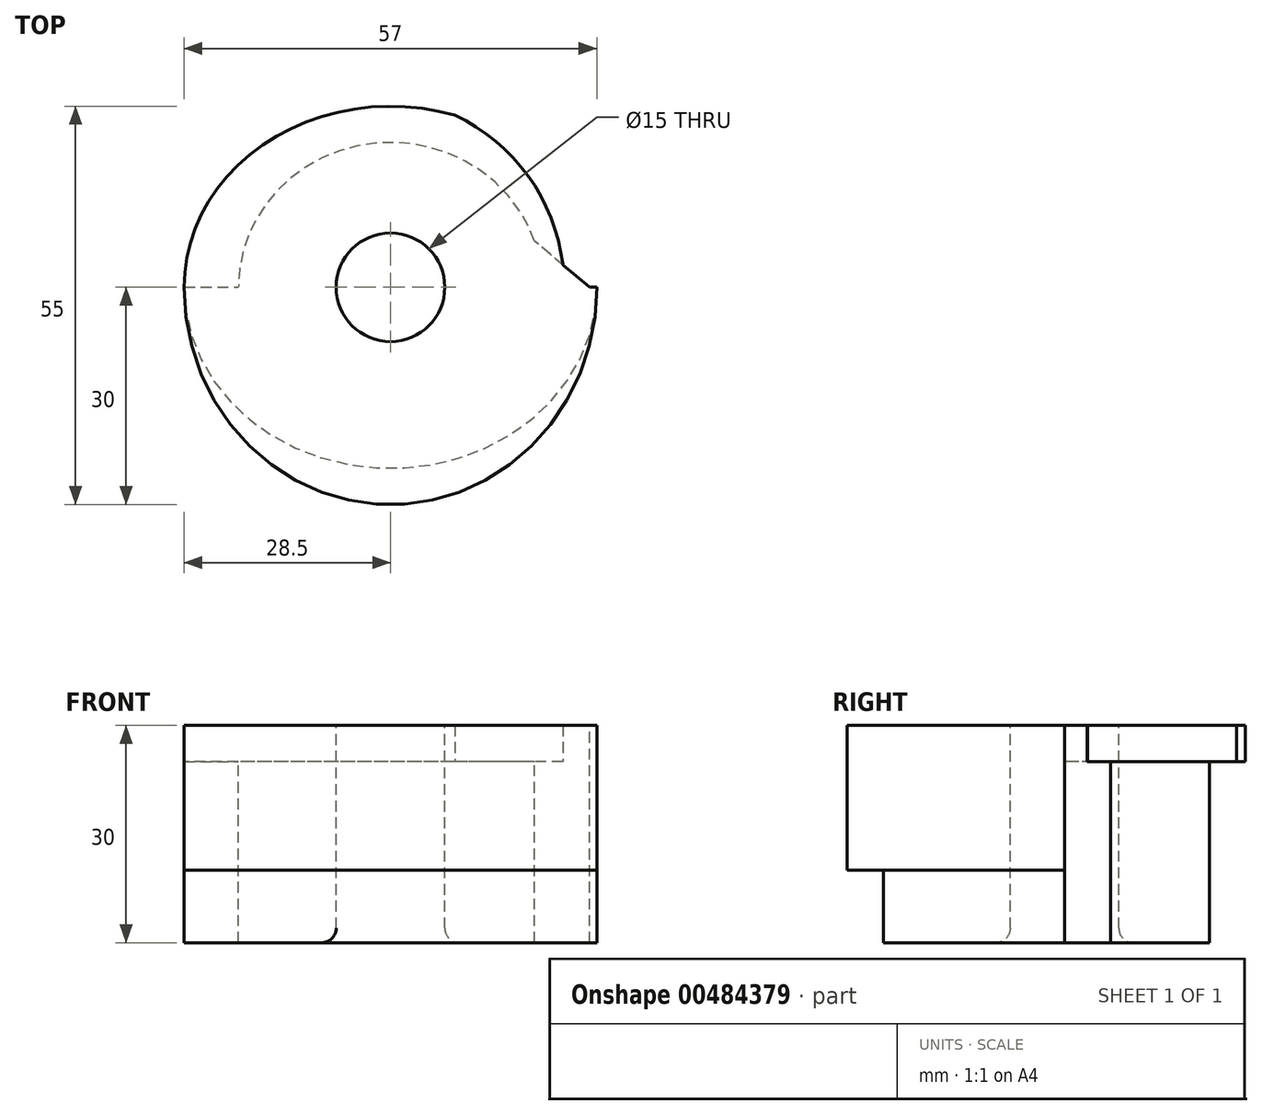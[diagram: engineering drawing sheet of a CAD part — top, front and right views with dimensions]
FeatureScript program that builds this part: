
annotation { "Feature Type Name" : "Feature", "Feature Type Description" : "" }
export const myFeature = defineFeature(function(context is Context, id is Id, definition is map)
    precondition{}
    {
        {
            var Q0;
            Q0=qCreatedBy(makeId("Top.planeOp"),FACE);
            var sketch = newSketch(context, id + "F0", { "sketchPlane" : qUnion([Q0])});
            skEllipse(sketch, "E0", {"center": v(0, 0) * mm, "majorRadius": 28.5 * mm, "minorRadius": 25 * mm, "majorAxis": v(1, 0)});
            skEllipse(sketch, "E1", {"center": v(0, 0) * mm, "majorRadius": 21 * mm, "minorRadius": 20 * mm, "majorAxis": v(-1, 0)});
            skLineSegment(sketch, "E2", {"start": v(-28.5, 0) * mm, "end": v(-21, 0) * mm});
            skLineSegment(sketch, "E3", {"start": v(27.5, 0) * mm, "end": v(19.9, 6.37) * mm});
            skLineSegment(sketch, "E4", {"start": v(21, 0) * mm, "end": v(28.5, 0) * mm});
            skCircle(sketch, "E5", {"center": v(0, 0) * mm, "radius": 7.5 * mm});
            skEllipse(sketch, "E6", {"center": v(0, 0) * mm, "majorRadius": 28.5 * mm, "minorRadius": 30 * mm, "majorAxis": v(1, 0)});
            skEllipse(sketch, "E7", {"center": v(0, 0) * mm, "majorRadius": 24 * mm, "minorRadius": 24 * mm, "majorAxis": v(-1, 0)});
            skArc(sketch, "E8", {"start": v(23.79, 3.19) * mm, "mid": v(-3.86, 26.2) * mm, "end": v(-28.5, 0) * mm});
            skPoint(sketch, "E8.startSnap0", {"position": v(23.7, 3.19) * mm});
            skSolve(sketch);
        }
        {
            var Q0;
            {var subQ0=sQuery(id+"F0.wireOp",EDGE,"E1");var subQ1=makeQuery(id+"F0.imprint","INTERSECT",VERTEX,{"derivedFrom":[subQ0,sQuery(id+"F0.wireOp",EDGE,"E2")]});Q0=makeQuery(id+"F0.imprint","IMPRINT",FACE,{"disambiguationData":[TD([[makeQuery(id+"F0.imprint","IMPRINT",EDGE,{"disambiguationData":[TD([[subQ1,-1.0]])],"derivedFrom":subQ0}),1.0]])]});}
            var Q1;
            {var subQ0=sQuery(id+"F0.wireOp",EDGE,"E2");Q1=makeQuery(id+"F0.imprint","IMPRINT",FACE,{"disambiguationData":[TD([[makeQuery(id+"F0.imprint","IMPRINT",EDGE,{"derivedFrom":subQ0}),-1.0]])]});}
            var Q2;
            {var subQ0=sQuery(id+"F0.wireOp",EDGE,"E3");Q2=makeQuery(id+"F0.imprint","IMPRINT",FACE,{"disambiguationData":[TD([[makeQuery(id+"F0.imprint","IMPRINT",EDGE,{"derivedFrom":subQ0}),1.0]])]});}
            var Q3;
            {var subQ0=sQuery(id+"F0.wireOp",EDGE,"E3");var subQ1=sQuery(id+"F0.wireOp",EDGE,"E1");var subQ2=makeQuery(id+"F0.imprint","INTERSECT",VERTEX,{"derivedFrom":[subQ1,subQ0]});Q3=makeQuery(id+"F0.imprint","IMPRINT",FACE,{"disambiguationData":[TD([[makeQuery(id+"F0.imprint","IMPRINT",EDGE,{"disambiguationData":[TD([[subQ2,1.0]])],"derivedFrom":subQ1}),-1.0]])]});}
            var Q4;
            {var subQ0=sQuery(id+"F0.wireOp",EDGE,"E4");var subQ1=makeQuery(id+"F0.imprint","INTERSECT",VERTEX,{"derivedFrom":[sQuery(id+"F0.wireOp",EDGE,"E3"),subQ0]});Q4=makeQuery(id+"F0.imprint","IMPRINT",FACE,{"disambiguationData":[TD([[makeQuery(id+"F0.imprint","IMPRINT",EDGE,{"disambiguationData":[TD([[subQ1,1.0]])],"derivedFrom":subQ0}),-1.0]])]});}
            var Q5;
            {var subQ0=sQuery(id+"F0.wireOp",EDGE,"E4");var subQ1=sQuery(id+"F0.wireOp",EDGE,"E3");var subQ2=makeQuery(id+"F0.imprint","INTERSECT",VERTEX,{"derivedFrom":[subQ1,subQ0]});Q5=makeQuery(id+"F0.imprint","IMPRINT",FACE,{"disambiguationData":[TD([[makeQuery(id+"F0.imprint","IMPRINT",EDGE,{"disambiguationData":[TD([[subQ2,-1.0]])],"derivedFrom":subQ1}),1.0]])]});}
            extrude(context, id + "F1", {"entities" : qUnion([Q0, Q1, Q2, Q3, Q4, Q5]), "oppositeDirection" : true, "depth" : 10 * mm, "offsetDistance" : 25 * mm});
        }
        {
            var Q0;
            {var subQ0=sQuery(id+"F0.wireOp",EDGE,"E6");var subQ1=sQuery(id+"F0.wireOp",EDGE,"E0");var subQ2=makeQuery(id+"F0.imprint","INTERSECT",VERTEX,{"derivedFrom":[subQ1,sQuery(id+"F0.wireOp",EDGE,"E2"),subQ0]});Q0=makeQuery(id+"F0.imprint","IMPRINT",FACE,{"disambiguationData":[TD([[makeQuery(id+"F0.imprint","IMPRINT",EDGE,{"disambiguationData":[TD([[subQ2,-1.0]])],"derivedFrom":subQ1}),-1.0]])]});}
            var Q1;
            {var subQ0=sQuery(id+"F0.wireOp",EDGE,"E4");var subQ1=makeQuery(id+"F0.imprint","INTERSECT",VERTEX,{"derivedFrom":[sQuery(id+"F0.wireOp",EDGE,"E3"),subQ0]});Q1=makeQuery(id+"F0.imprint","IMPRINT",FACE,{"disambiguationData":[TD([[makeQuery(id+"F0.imprint","IMPRINT",EDGE,{"disambiguationData":[TD([[subQ1,1.0]])],"derivedFrom":subQ0}),-1.0]])]});}
            var Q2;
            {var subQ0=sQuery(id+"F0.wireOp",EDGE,"E2");var subQ1=sQuery(id+"F0.wireOp",EDGE,"E1");var subQ2=makeQuery(id+"F0.imprint","INTERSECT",VERTEX,{"derivedFrom":[subQ1,subQ0]});Q2=makeQuery(id+"F0.imprint","IMPRINT",FACE,{"disambiguationData":[TD([[makeQuery(id+"F0.imprint","IMPRINT",EDGE,{"disambiguationData":[TD([[subQ2,1.0]])],"derivedFrom":subQ1}),-1.0]])]});}
            var Q3;
            {var subQ0=sQuery(id+"F0.wireOp",EDGE,"E2");var subQ1=sQuery(id+"F0.wireOp",EDGE,"E1");var subQ2=makeQuery(id+"F0.imprint","INTERSECT",VERTEX,{"derivedFrom":[subQ1,subQ0]});Q3=makeQuery(id+"F0.imprint","IMPRINT",FACE,{"disambiguationData":[TD([[makeQuery(id+"F0.imprint","IMPRINT",EDGE,{"disambiguationData":[TD([[subQ2,-1.0]])],"derivedFrom":subQ1}),-1.0]])]});}
            var Q4;
            Q4=makeQuery(id+"F0.imprint","IMPRINT",FACE,{"disambiguationData":[TD([[makeQuery(id+"F0.imprint","IMPRINT",EDGE,{"derivedFrom":sQuery(id+"F0.wireOp",EDGE,"E5")}),-1.0]])]});
            var Q5;
            {var subQ0=sQuery(id+"F0.wireOp",EDGE,"E3");var subQ1=sQuery(id+"F0.wireOp",EDGE,"E1");var subQ2=makeQuery(id+"F0.imprint","INTERSECT",VERTEX,{"derivedFrom":[subQ1,subQ0]});Q5=makeQuery(id+"F0.imprint","IMPRINT",FACE,{"disambiguationData":[TD([[makeQuery(id+"F0.imprint","IMPRINT",EDGE,{"disambiguationData":[TD([[subQ2,1.0]])],"derivedFrom":subQ1}),-1.0]])]});}
            var Q6;
            {var subQ0=sQuery(id+"F0.wireOp",EDGE,"E4");var subQ1=sQuery(id+"F0.wireOp",EDGE,"E3");var subQ2=makeQuery(id+"F0.imprint","INTERSECT",VERTEX,{"derivedFrom":[subQ1,subQ0]});Q6=makeQuery(id+"F0.imprint","IMPRINT",FACE,{"disambiguationData":[TD([[makeQuery(id+"F0.imprint","IMPRINT",EDGE,{"disambiguationData":[TD([[subQ2,-1.0]])],"derivedFrom":subQ1}),1.0]])]});}
            var Q7;
            {var subQ0=sQuery(id+"F0.wireOp",EDGE,"E8");var subQ5=sQuery(id+"F0.wireOp",EDGE,"E7");var subQ7=makeQuery(id+"F0.imprint","INTERSECT",VERTEX,{"derivedFrom":[subQ5,subQ0]});Q7=makeQuery(id+"F0.imprint","IMPRINT",FACE,{"disambiguationData":[TD([[makeQuery(id+"F0.imprint","IMPRINT",EDGE,{"disambiguationData":[TD([[subQ7,-1.0]])],"derivedFrom":subQ5}),-1.0]])]});}
            extrude(context, id + "F2", {"entities" : qUnion([Q0, Q1, Q2, Q3, Q4, Q5, Q6, Q7]), "operationType" : NewBodyOperationType.ADD, "depth" : 20 * mm, "offsetDistance" : 25 * mm});
        }
        {
            var Q0;
            Q0=makeQuery(id+"F1.opExtrude","CAP_EDGE",EDGE,{"disambiguationData":[OSD([sQuery(id+"F0.wireOp",EDGE,"E5")])],"isStart":false});
            fillet(context, id + "F3", {"entities" : qUnion([Q0]), "radius" : 2 * mm, "tangentPropagation" : true, "allowEdgeOverflow" : false});
        }
        {
            var Q0;
            {var subQ4=sQuery(id+"F0.wireOp",EDGE,"E2");var subQ5=sQuery(id+"F0.wireOp",EDGE,"E1");var subQ6=makeQuery(id+"F0.imprint","INTERSECT",VERTEX,{"derivedFrom":[subQ5,subQ4]});Q0=makeQuery(id+"F0.imprint","IMPRINT",FACE,{"disambiguationData":[TD([[makeQuery(id+"F0.imprint","IMPRINT",EDGE,{"disambiguationData":[TD([[subQ6,1.0]])],"derivedFrom":subQ5}),-1.0]])]});}
            var Q1;
            {var subQ0=sQuery(id+"F0.wireOp",EDGE,"E8");var subQ5=sQuery(id+"F0.wireOp",EDGE,"E7");var subQ7=makeQuery(id+"F0.imprint","INTERSECT",VERTEX,{"derivedFrom":[subQ5,subQ0]});Q1=makeQuery(id+"F0.imprint","IMPRINT",FACE,{"disambiguationData":[TD([[makeQuery(id+"F0.imprint","IMPRINT",EDGE,{"disambiguationData":[TD([[subQ7,-1.0]])],"derivedFrom":subQ5}),-1.0]])]});}
            extrude(context, id + "F4", {"entities" : qUnion([Q0, Q1]), "operationType" : NewBodyOperationType.REMOVE, "depth" : 15 * mm, "offsetDistance" : 25 * mm});
        }
    });
